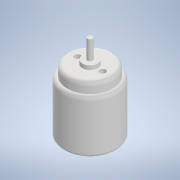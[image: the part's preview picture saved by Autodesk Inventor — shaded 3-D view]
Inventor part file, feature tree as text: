
AUTODESK INVENTOR PART (.ipt)
format: ipt  version: 2022 (Build 260153070, 153G)  size: 175,104 bytes
history: native  units: in
note: dims shown in document units (in); Inventor stores cm internally (conversion verified against a paired STEP export)
features: sketch x3, extrude x2, revolve x1, fillet x1, projected_geometry x1
ambient origin geometry x8: Origin, YZ Plane, XZ Plane, XY Plane, X Axis, Y Axis, Z Axis, Center Point
bodies: Body1 (feature_tree)
feature tree (8):
  revolve  "Revolution1"  [1 undecoded]
  fillet  "Fillet1"  Radius=0.0394in
  extrude  "Extrusion2"  TaperAngle=90.0deg  [1 undecoded]
  extrude  "Extrusion4"  Depth=0.1181in
  sketch  "Sketch3"  dims[d5=0.1673in d7=0.063in d10=0.0394in]
  sketch  "Sketch4"  dims[d13=0.0787in d14=90.0deg]
  sketch  "Sketch6"  dims[d15=0.0591in d16=0.1181in d17=0.315in d18=0.9843in d19=0.0591in d20=0.1575in d21=0.4134in d23=0.2461in d24=0.3937in d25=0.0906in d26=0.7874in d28=360.0deg d30=0.0787in d31=0.0in d34=0.0394in d35=0.0in]
  projected_geometry  "Projected Loop1"
note: 2 required parameter values undecoded (feature->parameter linkage not recoverable at this tier; creation-order binding heuristic only, values carry confidence <= 0.55)